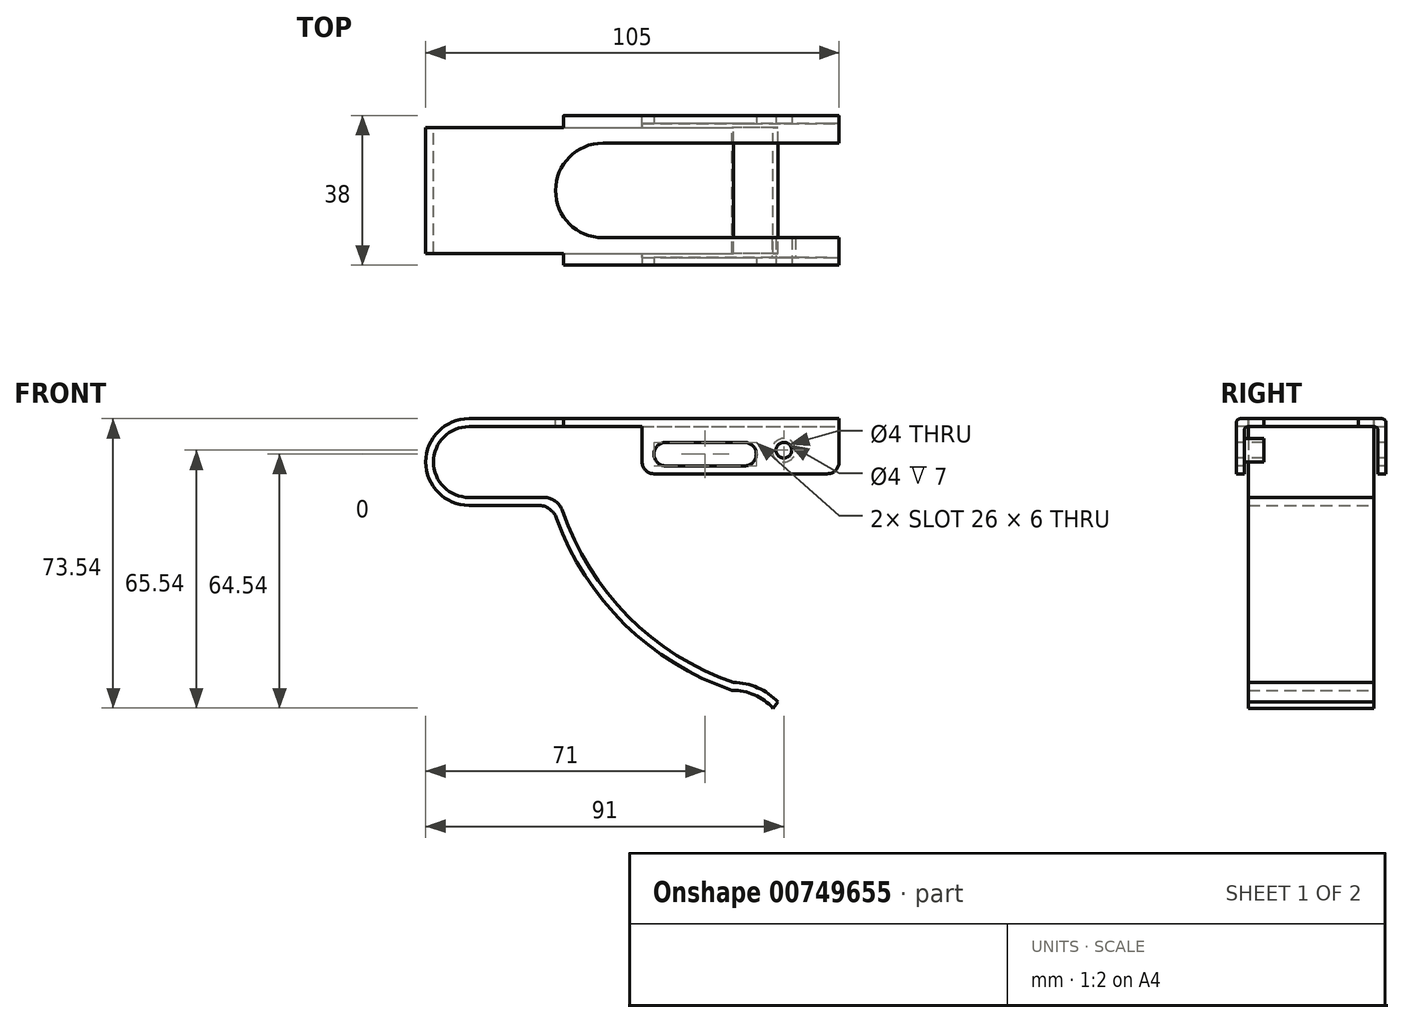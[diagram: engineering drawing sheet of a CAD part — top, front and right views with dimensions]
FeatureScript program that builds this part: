
annotation { "Feature Type Name" : "Feature", "Feature Type Description" : "" }
export const myFeature = defineFeature(function(context is Context, id is Id, definition is map)
    precondition{}
    {
        {
            var Q0;
            Q0=qCreatedBy(makeId("Front.planeOp"),FACE);
            var sketch = newSketch(context, id + "F0", { "sketchPlane" : qUnion([Q0])});
            skArc(sketch, "E0", {"start": v(0, 11) * mm, "mid": v(-11, 0) * mm, "end": v(0, -11) * mm});
            skLineSegment(sketch, "E1", {"start": v(0, 11) * mm, "end": v(94, 11) * mm});
            skLineSegment(sketch, "E2", {"start": v(0, -11) * mm, "end": v(17.58, -11) * mm});
            skArc(sketch, "E3", {"start": v(22.28, -14.3) * mm, "mid": v(39.57, -41.22) * mm, "end": v(66.81, -58) * mm});
            skArc(sketch, "E4", {"start": v(77.24, -62.54) * mm, "mid": v(72.51, -59.16) * mm, "end": v(66.81, -58) * mm});
            skPoint(sketch, "E5.visualSharp", {"position": v(21.18, -11) * mm});
            skArc(sketch, "E5.filletArc", {"start": v(22.28, -14.3) * mm, "mid": v(20.45, -11.9) * mm, "end": v(17.58, -11) * mm});
            skArc(sketch, "E6.0", {"start": v(78.54, -61) * mm, "mid": v(73.35, -57.35) * mm, "end": v(67.15, -56) * mm});
            skLineSegment(sketch, "E6.1", {"start": v(0, 9) * mm, "end": v(94, 9) * mm});
            skArc(sketch, "E6.2", {"start": v(0, 9) * mm, "mid": v(-9, 0) * mm, "end": v(0, -9) * mm});
            skLineSegment(sketch, "E6.3", {"start": v(0, -9) * mm, "end": v(19, -9) * mm});
            skArc(sketch, "E6.4", {"start": v(23.73, -12.39) * mm, "mid": v(40.4, -39.22) * mm, "end": v(67.15, -56) * mm});
            skPoint(sketch, "E7.visualSharp", {"position": v(22.67, -9) * mm});
            skArc(sketch, "E7.filletArc", {"start": v(23.73, -12.39) * mm, "mid": v(21.91, -9.93) * mm, "end": v(19, -9) * mm});
            skLineSegment(sketch, "E8", {"start": v(77.24, -62.54) * mm, "end": v(78.54, -61) * mm});
            skLineSegment(sketch, "E9", {"start": v(94, 9) * mm, "end": v(94, 11) * mm});
            skSolve(sketch);
        }
        {
            var Q0;
            Q0=qSketchRegion(id+"F0",true);
            extrude(context, id + "F1", {"entities" : qUnion([Q0]), "depth" : 16 * mm, "offsetDistance" : 25 * mm});
        }
        {
            var Q0;
            Q0=makeQuery(id+"F1.opExtrude","SWEPT_FACE",FACE,{"disambiguationData":[OSD([sQuery(id+"F0.wireOp",EDGE,"E1")])]});
            var sketch = newSketch(context, id + "F2", { "sketchPlane" : qUnion([Q0])});
            skLineSegment(sketch, "E10.bottom", {"start": v(94, -16) * mm, "end": v(24, -16) * mm});
            skLineSegment(sketch, "E10.top", {"start": v(94, -19) * mm, "end": v(24, -19) * mm});
            skLineSegment(sketch, "E10.left", {"start": v(94, -16) * mm, "end": v(94, -19) * mm});
            skLineSegment(sketch, "E10.right", {"start": v(24, -16) * mm, "end": v(24, -19) * mm});
            skSolve(sketch);
        }
        {
            var Q0;
            Q0=makeQuery(id+"F2.imprint","IMPRINT",FACE,{"disambiguationData":[TD([[makeQuery(id+"F2.imprint","IMPRINT",EDGE,{"derivedFrom":sQuery(id+"F2.wireOp",EDGE,"E10.bottom")}),-1.0]])]});
            extrude(context, id + "F3", {"entities" : qUnion([Q0]), "operationType" : NewBodyOperationType.ADD, "oppositeDirection" : true, "depth" : 2 * mm, "offsetDistance" : 25 * mm});
        }
        {
            var Q0;
            Q0=makeQuery(id+"F3.opExtrude","SWEPT_FACE",FACE,{"disambiguationData":[OSD([sQuery(id+"F2.wireOp",EDGE,"E10.top")])]});
            var sketch = newSketch(context, id + "F4", { "sketchPlane" : qUnion([Q0])});
            skLineSegment(sketch, "E11.bottom", {"start": v(94, 11) * mm, "end": v(44, 11) * mm});
            skLineSegment(sketch, "E11.top", {"start": v(94, -3) * mm, "end": v(44, -3) * mm});
            skLineSegment(sketch, "E11.left", {"start": v(94, 11) * mm, "end": v(94, -3) * mm});
            skLineSegment(sketch, "E11.right", {"start": v(44, 11) * mm, "end": v(44, -3) * mm});
            skSolve(sketch);
        }
        {
            var Q0;
            Q0=qSketchRegion(id+"F4",true);
            extrude(context, id + "F5", {"entities" : qUnion([Q0]), "operationType" : NewBodyOperationType.ADD, "oppositeDirection" : true, "depth" : 2 * mm, "offsetDistance" : 25 * mm});
        }
        {
            var Q0;
            Q0=makeQuery(id+"F3.opExtrude","CAP_EDGE",EDGE,{"disambiguationData":[OSD([sQuery(id+"F2.wireOp",EDGE,"E10.top")])],"isStart":true});
            var Q1;
            Q1=makeQuery(id+"F5.boolean.opBoolean","INTERSECT",EDGE,{"derivedFrom":[makeQuery(id+"F3.boolean.opBoolean","MERGE",FACE,{"derivedFrom":[makeQuery(id+"F1.opExtrude","SWEPT_FACE",FACE,{"disambiguationData":[OSD([sQuery(id+"F0.wireOp",EDGE,"E6.1")])]}),makeQuery(id+"F3.opExtrude","CAP_FACE",FACE,{"disambiguationData":[OSD([sQuery(id+"F2.wireOp",EDGE,"E10.bottom"),sQuery(id+"F2.wireOp",EDGE,"E10.top"),sQuery(id+"F2.wireOp",EDGE,"E10.left"),sQuery(id+"F2.wireOp",EDGE,"E10.right")])],"isStart":false})]}),makeQuery(id+"F5.opExtrude","CAP_FACE",FACE,{"disambiguationData":[OSD([sQuery(id+"F4.wireOp",EDGE,"E11.bottom"),sQuery(id+"F4.wireOp",EDGE,"E11.top"),sQuery(id+"F4.wireOp",EDGE,"E11.left"),sQuery(id+"F4.wireOp",EDGE,"E11.right")])],"isStart":false})]});
            fillet(context, id + "F6", {"entities" : qUnion([Q0, Q1]), "radius" : 1 * mm, "allowEdgeOverflow" : false});
        }
        {
            var Q0;
            Q0=makeQuery(id+"F1.opExtrude","SWEPT_BODY",BODY,{"disambiguationData":[OSD([sQuery(id+"F0.wireOp",EDGE,"E0"),sQuery(id+"F0.wireOp",EDGE,"E1"),sQuery(id+"F0.wireOp",EDGE,"E2"),sQuery(id+"F0.wireOp",EDGE,"E3"),sQuery(id+"F0.wireOp",EDGE,"E4"),sQuery(id+"F0.wireOp",EDGE,"E5.filletArc"),sQuery(id+"F0.wireOp",EDGE,"E6.0"),sQuery(id+"F0.wireOp",EDGE,"E6.1"),sQuery(id+"F0.wireOp",EDGE,"E6.2"),sQuery(id+"F0.wireOp",EDGE,"E6.3"),sQuery(id+"F0.wireOp",EDGE,"E6.4"),sQuery(id+"F0.wireOp",EDGE,"E7.filletArc"),sQuery(id+"F0.wireOp",EDGE,"E8"),sQuery(id+"F0.wireOp",EDGE,"E9")])]});
            var Q1;
            Q1=qCreatedBy(makeId("Front.planeOp"),FACE);
            mirror(context, id + "F7", {"operationType" : NewBodyOperationType.ADD, "entities" : qUnion([Q0]), "mirrorPlane" : qUnion([Q1])});
        }
        {
            var Q0;
            {var subQ0=makeQuery(id+"F3.boolean.opBoolean","MERGE",FACE,{"derivedFrom":[makeQuery(id+"F1.opExtrude","SWEPT_FACE",FACE,{"disambiguationData":[OSD([sQuery(id+"F0.wireOp",EDGE,"E1")])]}),makeQuery(id+"F3.opExtrude","CAP_FACE",FACE,{"disambiguationData":[OSD([sQuery(id+"F2.wireOp",EDGE,"E10.bottom"),sQuery(id+"F2.wireOp",EDGE,"E10.top"),sQuery(id+"F2.wireOp",EDGE,"E10.left"),sQuery(id+"F2.wireOp",EDGE,"E10.right")])],"isStart":true})]});Q0=makeQuery(id+"F7.boolean.opBoolean","MERGE",FACE,{"derivedFrom":[subQ0,makeQuery(id+"F7.opPattern","COPY",FACE,{"derivedFrom":subQ0,"instanceName":"1"})]});}
            var sketch = newSketch(context, id + "F8", { "sketchPlane" : qUnion([Q0])});
            skArc(sketch, "E12", {"start": v(34, 12) * mm, "mid": v(22, 0) * mm, "end": v(34, -12) * mm});
            skLineSegment(sketch, "E13", {"start": v(34, 12) * mm, "end": v(94, 12) * mm});
            skLineSegment(sketch, "E14", {"start": v(34, -12) * mm, "end": v(94, -12) * mm});
            skLineSegment(sketch, "E15", {"start": v(94, -12) * mm, "end": v(94, 12) * mm});
            skSolve(sketch);
        }
        {
            var Q0;
            Q0=qSketchRegion(id+"F8",true);
            extrude(context, id + "F9", {"entities" : qUnion([Q0]), "operationType" : NewBodyOperationType.REMOVE, "oppositeDirection" : true, "depth" : 2 * mm, "offsetDistance" : 25 * mm});
        }
        {
            var Q0;
            Q0=makeQuery(id+"F5.boolean.opBoolean","MERGE",FACE,{"derivedFrom":[makeQuery(id+"F3.opExtrude","SWEPT_FACE",FACE,{"disambiguationData":[OSD([sQuery(id+"F2.wireOp",EDGE,"E10.top")])]}),makeQuery(id+"F5.opExtrude","CAP_FACE",FACE,{"disambiguationData":[OSD([sQuery(id+"F4.wireOp",EDGE,"E11.bottom"),sQuery(id+"F4.wireOp",EDGE,"E11.top"),sQuery(id+"F4.wireOp",EDGE,"E11.left"),sQuery(id+"F4.wireOp",EDGE,"E11.right")])],"isStart":true})]});
            var sketch = newSketch(context, id + "F10", { "sketchPlane" : qUnion([Q0])});
            skLineSegment(sketch, "E16", {"start": v(50, 2) * mm, "end": v(70, 2) * mm});
            skArc(sketch, "E17.0.startCap", {"start": v(50, -1) * mm, "mid": v(47, 2) * mm, "end": v(50, 5) * mm});
            skArc(sketch, "E17.0.endCap", {"start": v(70, 5) * mm, "mid": v(73, 2) * mm, "end": v(70, -1) * mm});
            skLineSegment(sketch, "E17.0.left", {"start": v(50, 5) * mm, "end": v(70, 5) * mm});
            skLineSegment(sketch, "E17.0.right", {"start": v(50, -1) * mm, "end": v(70, -1) * mm});
            skSolve(sketch);
        }
        {
            var Q0;
            Q0=qSketchRegion(id+"F10",true);
            extrude(context, id + "F11", {"entities" : qUnion([Q0]), "operationType" : NewBodyOperationType.REMOVE, "endBound" : BoundingType.THROUGH_ALL, "oppositeDirection" : true, "depth" : 25 * mm, "offsetDistance" : 25 * mm});
        }
        {
            var Q0;
            Q0=makeQuery(id+"F5.boolean.opBoolean","MERGE",FACE,{"derivedFrom":[makeQuery(id+"F3.opExtrude","SWEPT_FACE",FACE,{"disambiguationData":[OSD([sQuery(id+"F2.wireOp",EDGE,"E10.top")])]}),makeQuery(id+"F5.opExtrude","CAP_FACE",FACE,{"disambiguationData":[OSD([sQuery(id+"F4.wireOp",EDGE,"E11.bottom"),sQuery(id+"F4.wireOp",EDGE,"E11.top"),sQuery(id+"F4.wireOp",EDGE,"E11.left"),sQuery(id+"F4.wireOp",EDGE,"E11.right")])],"isStart":true})]});
            var sketch = newSketch(context, id + "F12", { "sketchPlane" : qUnion([Q0])});
            skPoint(sketch, "E18", {"position": v(80, 3) * mm});
            skSolve(sketch);
        }
        {
            var Q0;
            Q0=sQuery(id+"F12.wireOp",VERTEX,"E18");
            var Q1;
            Q1=makeQuery(id+"F1.opExtrude","SWEPT_BODY",BODY,{"disambiguationData":[OSD([sQuery(id+"F0.wireOp",EDGE,"E0"),sQuery(id+"F0.wireOp",EDGE,"E1"),sQuery(id+"F0.wireOp",EDGE,"E2"),sQuery(id+"F0.wireOp",EDGE,"E3"),sQuery(id+"F0.wireOp",EDGE,"E4"),sQuery(id+"F0.wireOp",EDGE,"E5.filletArc"),sQuery(id+"F0.wireOp",EDGE,"E6.0"),sQuery(id+"F0.wireOp",EDGE,"E6.1"),sQuery(id+"F0.wireOp",EDGE,"E6.2"),sQuery(id+"F0.wireOp",EDGE,"E6.3"),sQuery(id+"F0.wireOp",EDGE,"E6.4"),sQuery(id+"F0.wireOp",EDGE,"E7.filletArc"),sQuery(id+"F0.wireOp",EDGE,"E8"),sQuery(id+"F0.wireOp",EDGE,"E9")])]});
            hole(context, id + "F13", {"style" : HoleStyle.SIMPLE, "endStyle" : HoleEndStyle.THROUGH, "holeDiameter" : 4 * mm, "majorDiameter" : 5 * mm, "isTappedThrough" : true, "tappedDepth" : 12 * mm, "tapClearance" : 3, "locations" : qUnion([Q0]), "scope" : qUnion([Q1])});
        }
        {
            var Q0;
            Q0=makeQuery(id+"F5.opExtrude","CAP_FACE",FACE,{"disambiguationData":[OSD([sQuery(id+"F4.wireOp",EDGE,"E11.bottom"),sQuery(id+"F4.wireOp",EDGE,"E11.top"),sQuery(id+"F4.wireOp",EDGE,"E11.left"),sQuery(id+"F4.wireOp",EDGE,"E11.right")])],"isStart":false});
            var sketch = newSketch(context, id + "F14", { "sketchPlane" : qUnion([Q0])});
            skCircle(sketch, "E19.0", {"center": v(-80, 3) * mm, "radius": 2 * mm});
            skCircle(sketch, "E20.0", {"center": v(-80, 3) * mm, "radius": 3 * mm});
            skSolve(sketch);
        }
        {
            var Q0;
            Q0=qSketchRegion(id+"F14",true);
            extrude(context, id + "F15", {"entities" : qUnion([Q0]), "operationType" : NewBodyOperationType.ADD, "depth" : 5 * mm, "offsetDistance" : 25 * mm});
        }
        {
            var Q0;
            Q0=makeQuery(id+"F5.opExtrude","SWEPT_EDGE",EDGE,{"disambiguationData":[OSD([sQuery(id+"F4.wireOp",EDGE,"E11.top"),sQuery(id+"F4.wireOp",EDGE,"E11.right")])]});
            var Q1;
            Q1=makeQuery(id+"F5.opExtrude","SWEPT_EDGE",EDGE,{"disambiguationData":[OSD([sQuery(id+"F4.wireOp",EDGE,"E11.top"),sQuery(id+"F4.wireOp",EDGE,"E11.left")])]});
            var Q2;
            Q2=makeQuery(id+"F7.opPattern","COPY",EDGE,{"derivedFrom":makeQuery(id+"F5.opExtrude","SWEPT_EDGE",EDGE,{"disambiguationData":[OSD([sQuery(id+"F4.wireOp",EDGE,"E11.top"),sQuery(id+"F4.wireOp",EDGE,"E11.right")])]}),"instanceName":"1"});
            var Q3;
            Q3=makeQuery(id+"F7.opPattern","COPY",EDGE,{"derivedFrom":makeQuery(id+"F5.opExtrude","SWEPT_EDGE",EDGE,{"disambiguationData":[OSD([sQuery(id+"F4.wireOp",EDGE,"E11.top"),sQuery(id+"F4.wireOp",EDGE,"E11.left")])]}),"instanceName":"1"});
            fillet(context, id + "F16", {"entities" : qUnion([Q0, Q1, Q2, Q3]), "radius" : 3 * mm, "tangentPropagation" : true, "allowEdgeOverflow" : false});
        }
    });
